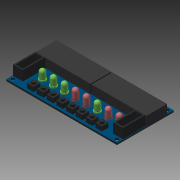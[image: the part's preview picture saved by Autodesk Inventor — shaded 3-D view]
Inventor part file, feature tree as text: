
AUTODESK INVENTOR PART (.ipt)
format: ipt  version: 2014 (Build 180170000, 170)  size: 311,808 bytes
history: native  units: in
note: dims shown in document units (in); Inventor stores cm internally (conversion verified against a paired STEP export)
features: extrude x8, sketch x8, pattern_linear x2, fillet x1
ambient origin geometry x8: Origin, YZ Plane, XZ Plane, XY Plane, X Axis, Y Axis, Z Axis, Center Point
bodies: Solid1 (feature_tree)
feature tree (19):
  extrude  "Extrusion1"  Depth=3.97in
  extrude  "Extrusion2"  Depth=0.06in
  extrude  "Extrusion3"  Depth=0.1181in
  extrude  "Extrusion4"  Depth=0.1181in
  extrude  "Extrusion5"  Depth=0.1181in
  pattern_linear  "Rectangular Pattern1"  Spacing1=0.1181in  [1 undecoded]
  extrude  "Extrusion6"  Depth=0.3488in
  fillet  "Fillet1"  Radius=0.06in
  extrude  "Extrusion7"  Depth=0.2362in
  pattern_linear  "Rectangular Pattern2"  Spacing1=0.2362in  [1 undecoded]
  extrude  "Extrusion8"  Depth=0.748in
  sketch  "Sketch1"  dims[d0=2.036in d1=3.97in]
  sketch  "Sketch2"  dims[d2=0.06in d3=0.0in d4=0.1181in]
  sketch  "Sketch3"  dims[d5=0.1181in d6=0.1181in]
  sketch  "Sketch4"  dims[d7=0.1181in d8=0.1181in]
  sketch  "Sketch5"  dims[d9=0.1181in d10=0.1181in]
  sketch  "Sketch6"  dims[d11=0.1181in]
  sketch  "Sketch7"  dims[d12=0.1181in]
  sketch  "Sketch8"  dims[d13=0.1181in d14=0.1181in d15=0.1181in d16=0.06in d17=0.0in d18=0.2362in d19=0.2362in d20=0.748in d21=1.9685in d22=1.9685in d23=0.315in d24=0.0in d25=0.2362in d26=0.2362in d27=0.0906in d28=0.6555in d29=0.1575in d30=0.0in d31=0.1358in d32=0.065in d33=0.0in d34=3.1496in d36=0.3496in d37=0.1969in d38=0.6693in d39=0.6299in d40=0.3543in d41=0.0in d42=0.0984in d43=0.2283in d44=0.0472in d45=0.0in d46=3.1496in d48=0.3937in d49=0.3543in d50=0.0157in d51=0.0157in d52=0.8071in d53=0.05in d54=0.05in d55=0.05in d56=0.05in d57=0.05in d58=0.0157in d59=0.3543in d60=0.05in d61=0.3488in d62=0.0in]
note: 2 required parameter values undecoded (feature->parameter linkage not recoverable at this tier; creation-order binding heuristic only, values carry confidence <= 0.55)
